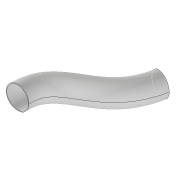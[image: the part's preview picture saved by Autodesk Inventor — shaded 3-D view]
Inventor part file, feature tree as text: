
AUTODESK INVENTOR PART (.ipt)
format: ipt  version: 2020 (Build 240168000, 168)  size: 343,040 bytes
history: native  units: mm
features: sketch x2, sweep x1
ambient origin geometry x8: Origin, YZ Plane, XZ Plane, XY Plane, X Axis, Y Axis, Z Axis, Center Point
bodies: Volumenkörper1 (feature_tree)
feature tree (3):
  sweep  "Sweeping1"
  sketch  "Skizze1"  dims[d0=170.0mm d1=180.0mm]
  sketch  "Skizze2"  dims[d2=0.0mm d3=0.0mm]
